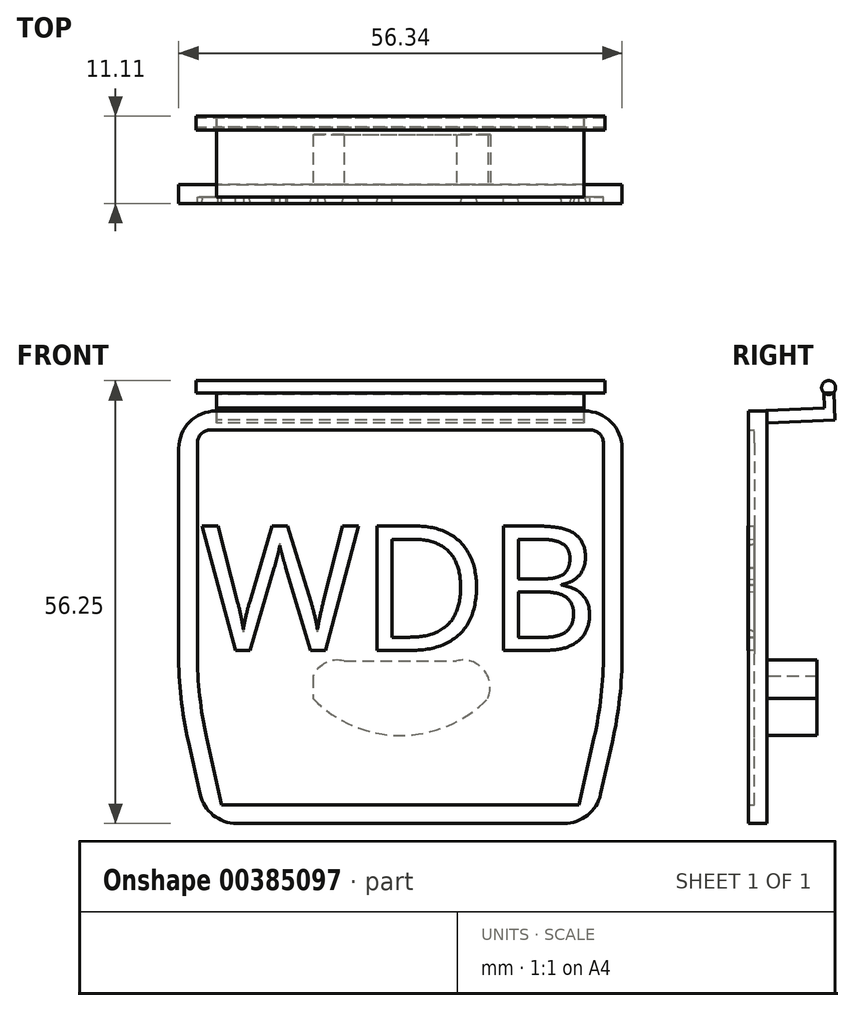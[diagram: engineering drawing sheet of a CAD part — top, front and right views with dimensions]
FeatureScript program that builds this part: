
annotation { "Feature Type Name" : "Feature", "Feature Type Description" : "" }
export const myFeature = defineFeature(function(context is Context, id is Id, definition is map)
    precondition{}
    {
        {
            var Q0;
            Q0=qCreatedBy(makeId("Front.planeOp"),FACE);
            var sketch = newSketch(context, id + "F0", { "sketchPlane" : qUnion([Q0])});
            skLineSegment(sketch, "E0", {"start": v(0, 0) * mm, "end": v(28.17, 0) * mm});
            skLineSegment(sketch, "E1", {"start": v(28.17, 5.63) * mm, "end": v(28.17, 31.75) * mm});
            skLineSegment(sketch, "E2", {"start": v(23.4, 36.51) * mm, "end": v(-23.4, 36.51) * mm});
            skLineSegment(sketch, "E3", {"start": v(-28.17, 31.75) * mm, "end": v(-28.17, 5.63) * mm});
            skLineSegment(sketch, "E4", {"start": v(-26.94, -5.5) * mm, "end": v(-25.44, -12.16) * mm});
            skLineSegment(sketch, "E5", {"start": v(-20.8, -15.88) * mm, "end": v(0, -15.88) * mm});
            skLineSegment(sketch, "E6", {"start": v(0, -15.88) * mm, "end": v(20.8, -15.88) * mm});
            skLineSegment(sketch, "E7", {"start": v(25.44, -12.16) * mm, "end": v(26.94, -5.5) * mm});
            skPoint(sketch, "E8.visualSharp", {"position": v(-28.17, 0) * mm});
            skArc(sketch, "E8.filletArc", {"start": v(-28.17, 5.63) * mm, "mid": v(-27.86, 0.03) * mm, "end": v(-26.94, -5.5) * mm});
            skPoint(sketch, "E9.visualSharp", {"position": v(28.17, 0) * mm});
            skArc(sketch, "E9.filletArc", {"start": v(26.94, -5.5) * mm, "mid": v(27.86, 0.03) * mm, "end": v(28.17, 5.63) * mm});
            skPoint(sketch, "E10.visualSharp", {"position": v(-28.17, 36.51) * mm});
            skArc(sketch, "E10.filletArc", {"start": v(-23.4, 36.51) * mm, "mid": v(-26.77, 35.12) * mm, "end": v(-28.17, 31.75) * mm});
            skPoint(sketch, "E11.visualSharp", {"position": v(28.17, 36.51) * mm});
            skArc(sketch, "E11.filletArc", {"start": v(28.17, 31.75) * mm, "mid": v(26.77, 35.12) * mm, "end": v(23.4, 36.51) * mm});
            skPoint(sketch, "E12.visualSharp", {"position": v(24.6, -15.88) * mm});
            skArc(sketch, "E12.filletArc", {"start": v(20.8, -15.87) * mm, "mid": v(23.77, -14.83) * mm, "end": v(25.44, -12.16) * mm});
            skPoint(sketch, "E13.visualSharp", {"position": v(-24.6, -15.88) * mm});
            skArc(sketch, "E13.filletArc", {"start": v(-25.44, -12.16) * mm, "mid": v(-23.77, -14.83) * mm, "end": v(-20.8, -15.87) * mm});
            skLineSegment(sketch, "E14.0", {"start": v(24.08, 34.13) * mm, "end": v(-24.08, 34.13) * mm});
            skLineSegment(sketch, "E14.1", {"start": v(25.79, 5.63) * mm, "end": v(25.79, 32.42) * mm});
            skLineSegment(sketch, "E14.2", {"start": v(-25.79, 32.42) * mm, "end": v(-25.79, 5.63) * mm});
            skArc(sketch, "E14.3", {"start": v(24.61, -4.97) * mm, "mid": v(25.5, 0.3) * mm, "end": v(25.79, 5.63) * mm});
            skLineSegment(sketch, "E14.4", {"start": v(22.7, -13.5) * mm, "end": v(24.61, -4.97) * mm});
            skArc(sketch, "E14.5", {"start": v(-25.79, 5.63) * mm, "mid": v(-25.5, 0.3) * mm, "end": v(-24.61, -4.97) * mm});
            skLineSegment(sketch, "E14.6", {"start": v(-24.61, -4.97) * mm, "end": v(-22.7, -13.5) * mm});
            skLineSegment(sketch, "E14.7", {"start": v(-22.7, -13.5) * mm, "end": v(0, -13.5) * mm});
            skLineSegment(sketch, "E14.8", {"start": v(0, -13.5) * mm, "end": v(22.7, -13.5) * mm});
            skPoint(sketch, "E15.visualSharp", {"position": v(-25.79, 34.13) * mm});
            skArc(sketch, "E15.filletArc", {"start": v(-24.08, 34.13) * mm, "mid": v(-25.29, 33.63) * mm, "end": v(-25.79, 32.42) * mm});
            skPoint(sketch, "E16.visualSharp", {"position": v(25.79, 34.13) * mm});
            skArc(sketch, "E16.filletArc", {"start": v(25.79, 32.42) * mm, "mid": v(25.29, 33.63) * mm, "end": v(24.08, 34.13) * mm});
            skLineSegment(sketch, "E17.bottom", {"start": v(-11.11, 4.76) * mm, "end": v(11.11, 4.76) * mm});
            skLineSegment(sketch, "E17.top", {"start": v(-11.11, -4.76) * mm, "end": v(11.11, -4.76) * mm});
            skLineSegment(sketch, "E17.left", {"start": v(-11.11, 4.76) * mm, "end": v(-11.11, -4.76) * mm});
            skLineSegment(sketch, "E17.right", {"start": v(11.11, 4.76) * mm, "end": v(11.11, -4.76) * mm});
            skPoint(sketch, "E17.middle", {"position": v(0, 0) * mm});
            skArc(sketch, "E18", {"start": v(-11.11, 0) * mm, "mid": v(0, -4.7) * mm, "end": v(11.11, 0) * mm});
            skArc(sketch, "E19", {"start": v(-7.14, 4.76) * mm, "mid": v(-10.61, 3.62) * mm, "end": v(-11.11, 0) * mm});
            skArc(sketch, "E20.MirrorCS", {"start": v(7.14, 4.76) * mm, "mid": v(10.61, 3.62) * mm, "end": v(11.11, 0) * mm});
            skLineSegment(sketch, "E21", {"start": v(7.14, 4.76) * mm, "end": v(-7.14, 4.76) * mm});
            skSolve(sketch);
        }
        {
            var Q0;
            {var subQ4=sQuery(id+"F0.wireOp",EDGE,"E1");Q0=makeQuery(id+"F0.imprint","IMPRINT",FACE,{"disambiguationData":[TD([[makeQuery(id+"F0.imprint","IMPRINT",EDGE,{"derivedFrom":subQ4}),1.0]])]});}
            var Q1;
            Q1=makeQuery(id+"F0.imprint","IMPRINT",FACE,{"disambiguationData":[TD([[makeQuery(id+"F0.imprint","IMPRINT",EDGE,{"derivedFrom":sQuery(id+"F0.wireOp",EDGE,"E14.0")}),1.0]])]});
            var Q2;
            {var subQ0=sQuery(id+"F0.wireOp",EDGE,"E20.MirrorCS");var subQ1=sQuery(id+"F0.wireOp",EDGE,"E17.right");var subQ3=makeQuery(id+"F0.imprint","INTERSECT",VERTEX,{"derivedFrom":[subQ1,subQ0]});Q2=makeQuery(id+"F0.imprint","IMPRINT",FACE,{"disambiguationData":[TD([[makeQuery(id+"F0.imprint","IMPRINT",EDGE,{"disambiguationData":[TD([[subQ3,-1.0]])],"derivedFrom":subQ1}),1.0]])]});}
            var Q3;
            {var subQ0=sQuery(id+"F0.wireOp",EDGE,"E20.MirrorCS");var subQ1=sQuery(id+"F0.wireOp",EDGE,"E17.bottom");var subQ2=makeQuery(id+"F0.imprint","INTERSECT",VERTEX,{"disambiguationData":[OD(0.0)],"derivedFrom":[subQ1,subQ0]});Q3=makeQuery(id+"F0.imprint","IMPRINT",FACE,{"disambiguationData":[TD([[makeQuery(id+"F0.imprint","IMPRINT",EDGE,{"disambiguationData":[TD([[subQ2,-1.0]])],"derivedFrom":subQ1}),-1.0]])]});}
            var Q4;
            {var subQ1=sQuery(id+"F0.wireOp",EDGE,"E18");Q4=makeQuery(id+"F0.imprint","IMPRINT",FACE,{"disambiguationData":[TD([[makeQuery(id+"F0.imprint","IMPRINT",EDGE,{"derivedFrom":subQ1}),1.0]])]});}
            var Q5;
            {var subQ0=sQuery(id+"F0.wireOp",EDGE,"E17.left");var subQ1=sQuery(id+"F0.wireOp",EDGE,"E17.bottom");var subQ2=makeQuery(id+"F0.imprint","INTERSECT",VERTEX,{"derivedFrom":[subQ1,subQ0]});Q5=makeQuery(id+"F0.imprint","IMPRINT",FACE,{"disambiguationData":[TD([[makeQuery(id+"F0.imprint","IMPRINT",EDGE,{"disambiguationData":[TD([[subQ2,-1.0]])],"derivedFrom":subQ1}),-1.0]])]});}
            var Q6;
            {var subQ0=sQuery(id+"F0.wireOp",EDGE,"E19");var subQ1=sQuery(id+"F0.wireOp",EDGE,"E17.bottom");var subQ2=makeQuery(id+"F0.imprint","INTERSECT",VERTEX,{"disambiguationData":[OD(0.0)],"derivedFrom":[subQ1,subQ0]});Q6=makeQuery(id+"F0.imprint","IMPRINT",FACE,{"disambiguationData":[TD([[makeQuery(id+"F0.imprint","IMPRINT",EDGE,{"disambiguationData":[TD([[subQ2,1.0]])],"derivedFrom":subQ1}),1.0]])]});}
            var Q7;
            {var subQ0=sQuery(id+"F0.wireOp",EDGE,"E19");var subQ1=sQuery(id+"F0.wireOp",EDGE,"E17.left");var subQ3=makeQuery(id+"F0.imprint","INTERSECT",VERTEX,{"derivedFrom":[subQ1,subQ0]});Q7=makeQuery(id+"F0.imprint","IMPRINT",FACE,{"disambiguationData":[TD([[makeQuery(id+"F0.imprint","IMPRINT",EDGE,{"disambiguationData":[TD([[subQ3,-1.0]])],"derivedFrom":subQ1}),-1.0]])]});}
            var Q8;
            {var subQ0=sQuery(id+"F0.wireOp",EDGE,"E17.top");Q8=makeQuery(id+"F0.imprint","IMPRINT",FACE,{"disambiguationData":[TD([[makeQuery(id+"F0.imprint","IMPRINT",EDGE,{"derivedFrom":subQ0}),1.0]])]});}
            var Q9;
            {var subQ0=sQuery(id+"F0.wireOp",EDGE,"E20.MirrorCS");var subQ1=sQuery(id+"F0.wireOp",EDGE,"E17.bottom");var subQ2=makeQuery(id+"F0.imprint","INTERSECT",VERTEX,{"disambiguationData":[OD(0.0)],"derivedFrom":[subQ1,subQ0]});Q9=makeQuery(id+"F0.imprint","IMPRINT",FACE,{"disambiguationData":[TD([[makeQuery(id+"F0.imprint","IMPRINT",EDGE,{"disambiguationData":[TD([[subQ2,1.0]])],"derivedFrom":subQ1}),1.0]])]});}
            extrude(context, id + "F1", {"entities" : qUnion([Q0, Q1, Q2, Q3, Q4, Q5, Q6, Q7, Q8, Q9]), "depth" : 1.59 * mm});
        }
        {
            var Q0;
            Q0=qCreatedBy(makeId("Right.planeOp"),FACE);
            var sketch = newSketch(context, id + "F2", { "sketchPlane" : qUnion([Q0])});
            skLineSegment(sketch, "E22.0.0", {"start": v(0, 31.75) * mm, "end": v(0, 36.51) * mm});
            skLineSegment(sketch, "E22.0.1", {"start": v(0, 36.51) * mm, "end": v(-1.59, 36.51) * mm});
            skLineSegment(sketch, "E22.0.2", {"start": v(-1.59, 36.51) * mm, "end": v(-1.59, 31.75) * mm});
            skLineSegment(sketch, "E22.0.3", {"start": v(-1.59, 31.75) * mm, "end": v(0, 31.75) * mm});
            skLineSegment(sketch, "E23", {"start": v(-1.59, 36.51) * mm, "end": v(7.3, 36.9) * mm});
            skLineSegment(sketch, "E24", {"start": v(7.3, 36.9) * mm, "end": v(7.36, 35.33) * mm});
            skLineSegment(sketch, "E25", {"start": v(7.36, 35.33) * mm, "end": v(0, 35) * mm});
            skLineSegment(sketch, "E26", {"start": v(0, 35) * mm, "end": v(-1.59, 36.51) * mm});
            skLineSegment(sketch, "E27", {"start": v(7.3, 36.9) * mm, "end": v(7.21, 38.8) * mm});
            skLineSegment(sketch, "E28", {"start": v(8.48, 38.86) * mm, "end": v(8.63, 35.38) * mm});
            skCircle(sketch, "E29", {"center": v(7.82, 39.48) * mm, "radius": 0.89 * mm});
            skLineSegment(sketch, "E30", {"start": v(7.36, 35.33) * mm, "end": v(8.63, 35.38) * mm});
            skLineSegment(sketch, "E31", {"start": v(7.21, 38.8) * mm, "end": v(8.48, 38.86) * mm});
            skPoint(sketch, "E32.orphan", {"position": v(8.5, 38.54) * mm});
            skSolve(sketch);
        }
        {
            var Q0;
            {var subQ0=sQuery(id+"F2.wireOp",EDGE,"E22.0.1");Q0=makeQuery(id+"F2.imprint","IMPRINT",FACE,{"disambiguationData":[TD([[makeQuery(id+"F2.imprint","IMPRINT",EDGE,{"derivedFrom":subQ0}),-1.0]])]});}
            var Q1;
            {var subQ6=sQuery(id+"F2.wireOp",EDGE,"E24");Q1=makeQuery(id+"F2.imprint","IMPRINT",FACE,{"disambiguationData":[TD([[makeQuery(id+"F2.imprint","IMPRINT",EDGE,{"derivedFrom":subQ6}),1.0]])]});}
            extrude(context, id + "F3", {"entities" : qUnion([Q0, Q1]), "operationType" : NewBodyOperationType.ADD, "depth" : 46.67 * mm, "symmetric" : true});
        }
        {
            var Q0;
            {var subQ0=sQuery(id+"F2.wireOp",EDGE,"E31");Q0=makeQuery(id+"F2.imprint","IMPRINT",FACE,{"disambiguationData":[TD([[makeQuery(id+"F2.imprint","IMPRINT",EDGE,{"derivedFrom":subQ0}),1.0]])]});}
            var Q1;
            {var subQ0=sQuery(id+"F2.wireOp",EDGE,"E31");var subQ1=sQuery(id+"F2.wireOp",EDGE,"E29");var subQ2=makeQuery(id+"F2.imprint","INTERSECT",VERTEX,{"disambiguationData":[OD(0.0)],"derivedFrom":[subQ1,subQ0]});Q1=makeQuery(id+"F2.imprint","IMPRINT",FACE,{"disambiguationData":[TD([[makeQuery(id+"F2.imprint","IMPRINT",EDGE,{"disambiguationData":[TD([[subQ2,-1.0]])],"derivedFrom":subQ1}),1.0]])]});}
            extrude(context, id + "F4", {"entities" : qUnion([Q0, Q1]), "operationType" : NewBodyOperationType.ADD, "depth" : 51.94 * mm, "symmetric" : true});
        }
        {
            var Q0;
            {var subQ4=sQuery(id+"F0.wireOp",EDGE,"E1");Q0=makeQuery(id+"F0.imprint","IMPRINT",FACE,{"disambiguationData":[TD([[makeQuery(id+"F0.imprint","IMPRINT",EDGE,{"derivedFrom":subQ4}),1.0]])]});}
            extrude(context, id + "F5", {"entities" : qUnion([Q0]), "operationType" : NewBodyOperationType.ADD, "depth" : 2.38 * mm});
        }
        {
            var Q0;
            {var subQ1=sQuery(id+"F0.wireOp",EDGE,"E18");Q0=makeQuery(id+"F0.imprint","IMPRINT",FACE,{"disambiguationData":[TD([[makeQuery(id+"F0.imprint","IMPRINT",EDGE,{"derivedFrom":subQ1}),1.0]])]});}
            var Q1;
            {var subQ0=sQuery(id+"F0.wireOp",EDGE,"E20.MirrorCS");var subQ1=sQuery(id+"F0.wireOp",EDGE,"E17.bottom");var subQ2=makeQuery(id+"F0.imprint","INTERSECT",VERTEX,{"disambiguationData":[OD(0.0)],"derivedFrom":[subQ1,subQ0]});Q1=makeQuery(id+"F0.imprint","IMPRINT",FACE,{"disambiguationData":[TD([[makeQuery(id+"F0.imprint","IMPRINT",EDGE,{"disambiguationData":[TD([[subQ2,1.0]])],"derivedFrom":subQ1}),1.0]])]});}
            var Q2;
            {var subQ0=sQuery(id+"F0.wireOp",EDGE,"E20.MirrorCS");var subQ1=sQuery(id+"F0.wireOp",EDGE,"E17.right");var subQ3=makeQuery(id+"F0.imprint","INTERSECT",VERTEX,{"derivedFrom":[subQ1,subQ0]});Q2=makeQuery(id+"F0.imprint","IMPRINT",FACE,{"disambiguationData":[TD([[makeQuery(id+"F0.imprint","IMPRINT",EDGE,{"disambiguationData":[TD([[subQ3,-1.0]])],"derivedFrom":subQ1}),1.0]])]});}
            var Q3;
            {var subQ0=sQuery(id+"F0.wireOp",EDGE,"E19");var subQ1=sQuery(id+"F0.wireOp",EDGE,"E17.bottom");var subQ2=makeQuery(id+"F0.imprint","INTERSECT",VERTEX,{"disambiguationData":[OD(0.0)],"derivedFrom":[subQ1,subQ0]});Q3=makeQuery(id+"F0.imprint","IMPRINT",FACE,{"disambiguationData":[TD([[makeQuery(id+"F0.imprint","IMPRINT",EDGE,{"disambiguationData":[TD([[subQ2,1.0]])],"derivedFrom":subQ1}),1.0]])]});}
            extrude(context, id + "F6", {"entities" : qUnion([Q0, Q1, Q2, Q3]), "operationType" : NewBodyOperationType.ADD, "oppositeDirection" : true, "depth" : 6.35 * mm});
        }
        {
            var Q0;
            Q0=makeQuery(id+"F1.opExtrude","CAP_FACE",FACE,{"disambiguationData":[OSD([sQuery(id+"F0.wireOp",EDGE,"E1"),sQuery(id+"F0.wireOp",EDGE,"E2"),sQuery(id+"F0.wireOp",EDGE,"E3"),sQuery(id+"F0.wireOp",EDGE,"E4"),sQuery(id+"F0.wireOp",EDGE,"E5"),sQuery(id+"F0.wireOp",EDGE,"E6"),sQuery(id+"F0.wireOp",EDGE,"E7"),sQuery(id+"F0.wireOp",EDGE,"E8.filletArc"),sQuery(id+"F0.wireOp",EDGE,"E9.filletArc"),sQuery(id+"F0.wireOp",EDGE,"E10.filletArc"),sQuery(id+"F0.wireOp",EDGE,"E11.filletArc"),sQuery(id+"F0.wireOp",EDGE,"E12.filletArc"),sQuery(id+"F0.wireOp",EDGE,"E13.filletArc")])],"isStart":false});
            cPlane(context, id + "F7", {"entities" : qUnion([Q0]), "cplaneType" : CPlaneType.OFFSET, "offset" : 0 * mm, "width" : 152.4 * mm, "height" : 152.4 * mm});
        }
        {
            var Q0;
            Q0=qCreatedBy(id+"F7.planeOp",FACE);
            var sketch = newSketch(context, id + "F8", { "sketchPlane" : qUnion([Q0])});
            skText(sketch, "E33", { "text": "WDB", "fontName": "OpenSans-Regular.ttf"});
            const initialGuessF8  = {"E33": [-0.0254, 0.00616, 1, 0, 0.01582]};
            skSetInitialGuess(sketch, initialGuessF8);
            skSolve(sketch);
        }
        {
            var Q0;
            Q0 = qSketchRegion(id + "F8", true);
            extrude(context, id + "F9", {"entities" : qUnion([Q0]), "operationType" : NewBodyOperationType.ADD, "depth" : 0.81 * mm, "hasDraft" : true, "draftAngle" : 3 * degree});
        }
    });
